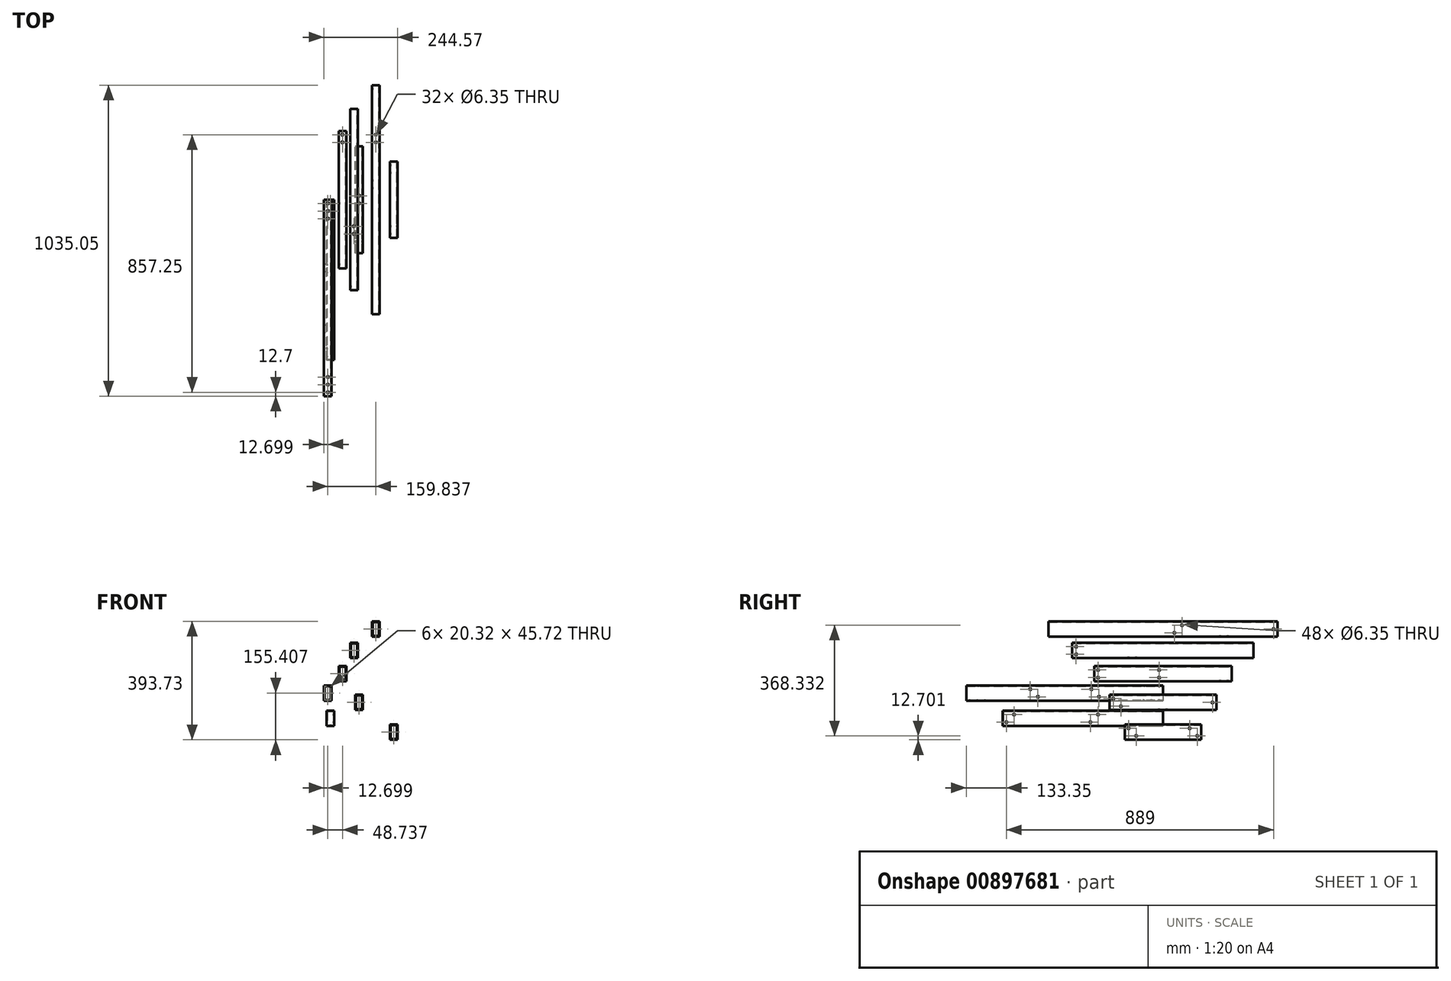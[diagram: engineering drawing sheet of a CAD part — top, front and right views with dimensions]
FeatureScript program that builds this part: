
annotation { "Feature Type Name" : "Feature", "Feature Type Description" : "" }
export const myFeature = defineFeature(function(context is Context, id is Id, definition is map)
    precondition{}
    {
        {
            var Q0;
            Q0=qCreatedBy(makeId("Front.planeOp"),FACE);
            var sketch = newSketch(context, id + "F0", { "sketchPlane" : qUnion([Q0])});
            skLineSegment(sketch, "E0.bottom", {"start": v(29.95, 32.2) * mm, "end": v(4.55, 32.2) * mm});
            skLineSegment(sketch, "E0.top", {"start": v(29.95, -18.6) * mm, "end": v(4.55, -18.6) * mm});
            skLineSegment(sketch, "E0.left", {"start": v(29.95, 32.2) * mm, "end": v(29.95, -18.6) * mm});
            skLineSegment(sketch, "E0.right", {"start": v(4.55, 32.2) * mm, "end": v(4.55, -18.6) * mm});
            skPoint(sketch, "E0.middle", {"position": v(17.25, 6.8) * mm});
            skSolve(sketch);
        }
        {
            var Q0;
            Q0 = qSketchRegion(id + "F0", true);
            extrude(context, id + "F1", {"entities" : qUnion([Q0]), "endBound" : BoundingType.SYMMETRIC, "depth" : 355.6 * mm, "offsetDistance" : 25.4 * mm});
        }
        {
            var Q0;
            Q0=makeQuery(id+"F1.opExtrude","CAP_FACE",FACE,{"disambiguationData":[OSD([sQuery(id+"F0.wireOp",EDGE,"E0.bottom"),sQuery(id+"F0.wireOp",EDGE,"E0.top"),sQuery(id+"F0.wireOp",EDGE,"E0.left"),sQuery(id+"F0.wireOp",EDGE,"E0.right")])],"isStart":false});
            var Q1;
            Q1=makeQuery(id+"F1.opExtrude","CAP_FACE",FACE,{"disambiguationData":[OSD([sQuery(id+"F0.wireOp",EDGE,"E0.bottom"),sQuery(id+"F0.wireOp",EDGE,"E0.top"),sQuery(id+"F0.wireOp",EDGE,"E0.left"),sQuery(id+"F0.wireOp",EDGE,"E0.right")])],"isStart":true});
            shell(context, id + "F2", {"entities" : qUnion([Q0, Q1]), "thickness" : 2.54 * mm});
        }
        {
            var Q0;
            Q0=qCreatedBy(makeId("Front.planeOp"),FACE);
            var sketch = newSketch(context, id + "F3", { "sketchPlane" : qUnion([Q0])});
            skLineSegment(sketch, "E1.bottom", {"start": v(-12.7, 205.12) * mm, "end": v(12.7, 205.12) * mm});
            skLineSegment(sketch, "E1.top", {"start": v(-12.7, 154.32) * mm, "end": v(12.7, 154.32) * mm});
            skLineSegment(sketch, "E1.left", {"start": v(-12.7, 205.12) * mm, "end": v(-12.7, 154.32) * mm});
            skLineSegment(sketch, "E1.right", {"start": v(12.7, 205.12) * mm, "end": v(12.7, 154.32) * mm});
            skPoint(sketch, "E1.middle", {"position": v(0, 179.72) * mm});
            skSolve(sketch);
        }
        {
            var Q0;
            Q0 = qSketchRegion(id + "F3", true);
            extrude(context, id + "F4", {"entities" : qUnion([Q0]), "endBound" : BoundingType.SYMMETRIC, "depth" : 603.25 * mm, "offsetDistance" : 25.4 * mm});
        }
        {
            var Q0;
            Q0=makeQuery(id+"F4.opExtrude","CAP_FACE",FACE,{"disambiguationData":[OSD([sQuery(id+"F3.wireOp",EDGE,"E1.bottom"),sQuery(id+"F3.wireOp",EDGE,"E1.top"),sQuery(id+"F3.wireOp",EDGE,"E1.left"),sQuery(id+"F3.wireOp",EDGE,"E1.right")])],"isStart":false});
            var Q1;
            Q1=makeQuery(id+"F4.opExtrude","CAP_FACE",FACE,{"disambiguationData":[OSD([sQuery(id+"F3.wireOp",EDGE,"E1.bottom"),sQuery(id+"F3.wireOp",EDGE,"E1.top"),sQuery(id+"F3.wireOp",EDGE,"E1.left"),sQuery(id+"F3.wireOp",EDGE,"E1.right")])],"isStart":true});
            shell(context, id + "F5", {"entities" : qUnion([Q0, Q1]), "thickness" : 2.54 * mm});
        }
        {
            var Q0;
            Q0=qCreatedBy(makeId("Front.planeOp"),FACE);
            var sketch = newSketch(context, id + "F6", { "sketchPlane" : qUnion([Q0])});
            skLineSegment(sketch, "E2.bottom", {"start": v(-25.48, 127.53) * mm, "end": v(-50.88, 127.53) * mm});
            skLineSegment(sketch, "E2.top", {"start": v(-25.48, 76.73) * mm, "end": v(-50.88, 76.73) * mm});
            skLineSegment(sketch, "E2.left", {"start": v(-25.48, 127.53) * mm, "end": v(-25.48, 76.73) * mm});
            skLineSegment(sketch, "E2.right", {"start": v(-50.88, 127.53) * mm, "end": v(-50.88, 76.73) * mm});
            skPoint(sketch, "E2.middle", {"position": v(-38.18, 102.13) * mm});
            skSolve(sketch);
        }
        {
            var Q0;
            Q0 = qSketchRegion(id + "F6", true);
            extrude(context, id + "F7", {"entities" : qUnion([Q0]), "endBound" : BoundingType.SYMMETRIC, "depth" : 457.2 * mm, "offsetDistance" : 25.4 * mm});
        }
        {
            var Q0;
            Q0=makeQuery(id+"F7.opExtrude","CAP_FACE",FACE,{"disambiguationData":[OSD([sQuery(id+"F6.wireOp",EDGE,"E2.bottom"),sQuery(id+"F6.wireOp",EDGE,"E2.top"),sQuery(id+"F6.wireOp",EDGE,"E2.left"),sQuery(id+"F6.wireOp",EDGE,"E2.right")])],"isStart":false});
            var Q1;
            Q1=makeQuery(id+"F7.opExtrude","CAP_FACE",FACE,{"disambiguationData":[OSD([sQuery(id+"F6.wireOp",EDGE,"E2.bottom"),sQuery(id+"F6.wireOp",EDGE,"E2.top"),sQuery(id+"F6.wireOp",EDGE,"E2.left"),sQuery(id+"F6.wireOp",EDGE,"E2.right")])],"isStart":true});
            shell(context, id + "F8", {"entities" : qUnion([Q0, Q1]), "thickness" : 2.54 * mm});
        }
        {
            var Q0;
            Q0=makeQuery(id+"F1.opExtrude","SWEPT_FACE",FACE,{"disambiguationData":[OSD([sQuery(id+"F0.wireOp",EDGE,"E0.left")])]});
            var sketch = newSketch(context, id + "F9", { "sketchPlane" : qUnion([Q0])});
            skCircle(sketch, "E3", {"center": v(-165.1, 19.5) * mm, "radius": 3.18 * mm});
            skCircle(sketch, "E4", {"center": v(-139.7, -5.9) * mm, "radius": 3.18 * mm});
            skCircle(sketch, "E5", {"center": v(165.1, 6.8) * mm, "radius": 3.18 * mm});
            skSolve(sketch);
        }
        {
            var Q0;
            Q0 = qSketchRegion(id + "F9", true);
            extrude(context, id + "F10", {"entities" : qUnion([Q0]), "operationType" : NewBodyOperationType.REMOVE, "endBound" : BoundingType.THROUGH_ALL, "oppositeDirection" : true, "depth" : 25.4 * mm, "offsetDistance" : 25.4 * mm});
        }
        {
            var Q0;
            Q0=makeQuery(id+"F1.opExtrude","SWEPT_FACE",FACE,{"disambiguationData":[OSD([sQuery(id+"F0.wireOp",EDGE,"E0.bottom")])]});
            var sketch = newSketch(context, id + "F11", { "sketchPlane" : qUnion([Q0])});
            skCircle(sketch, "E6", {"center": v(17.25, -12.7) * mm, "radius": 3.18 * mm});
            skCircle(sketch, "E7", {"center": v(17.25, 12.7) * mm, "radius": 3.18 * mm});
            skSolve(sketch);
        }
        {
            var Q0;
            Q0=makeQuery(id+"F11.imprint","IMPRINT",FACE,{"disambiguationData":[TD([[makeQuery(id+"F11.imprint","IMPRINT",EDGE,{"derivedFrom":sQuery(id+"F11.wireOp",EDGE,"E7")}),1.0]])]});
            var Q1;
            Q1=makeQuery(id+"F11.imprint","IMPRINT",FACE,{"disambiguationData":[TD([[makeQuery(id+"F11.imprint","IMPRINT",EDGE,{"derivedFrom":sQuery(id+"F11.wireOp",EDGE,"E6")}),1.0]])]});
            extrude(context, id + "F12", {"entities" : qUnion([Q0, Q1]), "operationType" : NewBodyOperationType.REMOVE, "endBound" : BoundingType.THROUGH_ALL, "oppositeDirection" : true, "depth" : 25.4 * mm, "offsetDistance" : 25.4 * mm});
        }
        {
            var Q0;
            Q0=makeQuery(id+"F4.opExtrude","SWEPT_FACE",FACE,{"disambiguationData":[OSD([sQuery(id+"F3.wireOp",EDGE,"E1.right")])]});
            var sketch = newSketch(context, id + "F13", { "sketchPlane" : qUnion([Q0])});
            skCircle(sketch, "E8", {"center": v(-288.93, 192.42) * mm, "radius": 3.18 * mm});
            skCircle(sketch, "E9", {"center": v(-288.93, 167.02) * mm, "radius": 3.18 * mm});
            skSolve(sketch);
        }
        {
            var Q0;
            Q0 = qSketchRegion(id + "F13", true);
            extrude(context, id + "F14", {"entities" : qUnion([Q0]), "operationType" : NewBodyOperationType.REMOVE, "endBound" : BoundingType.THROUGH_ALL, "oppositeDirection" : true, "depth" : 25.4 * mm, "offsetDistance" : 25.4 * mm});
        }
        {
            var Q0;
            Q0=makeQuery(id+"F4.opExtrude","SWEPT_FACE",FACE,{"disambiguationData":[OSD([sQuery(id+"F3.wireOp",EDGE,"E1.bottom")])]});
            var sketch = newSketch(context, id + "F15", { "sketchPlane" : qUnion([Q0])});
            skCircle(sketch, "E10", {"center": v(0, -114.3) * mm, "radius": 3.18 * mm});
            skCircle(sketch, "E11", {"center": v(0, -88.9) * mm, "radius": 3.18 * mm});
            skSolve(sketch);
        }
        {
            var Q0;
            Q0 = qSketchRegion(id + "F15", true);
            extrude(context, id + "F16", {"entities" : qUnion([Q0]), "operationType" : NewBodyOperationType.REMOVE, "endBound" : BoundingType.THROUGH_ALL, "oppositeDirection" : true, "depth" : 25.4 * mm, "offsetDistance" : 25.4 * mm});
        }
        {
            var Q0;
            Q0=makeQuery(id+"F7.opExtrude","SWEPT_FACE",FACE,{"disambiguationData":[OSD([sQuery(id+"F6.wireOp",EDGE,"E2.left")])]});
            var sketch = newSketch(context, id + "F17", { "sketchPlane" : qUnion([Q0])});
            skCircle(sketch, "E12", {"center": v(-215.9, 114.83) * mm, "radius": 3.18 * mm});
            skCircle(sketch, "E13", {"center": v(-215.9, 89.43) * mm, "radius": 3.18 * mm});
            skCircle(sketch, "E14", {"center": v(-12.7, 114.83) * mm, "radius": 3.18 * mm});
            skCircle(sketch, "E15", {"center": v(-12.7, 89.43) * mm, "radius": 3.18 * mm});
            skSolve(sketch);
        }
        {
            var Q0;
            Q0 = qSketchRegion(id + "F17", true);
            extrude(context, id + "F18", {"entities" : qUnion([Q0]), "operationType" : NewBodyOperationType.REMOVE, "endBound" : BoundingType.THROUGH_ALL, "oppositeDirection" : true, "depth" : 25.4 * mm, "offsetDistance" : 25.4 * mm});
        }
        {
            var Q0;
            Q0=makeQuery(id+"F7.opExtrude","SWEPT_FACE",FACE,{"disambiguationData":[OSD([sQuery(id+"F6.wireOp",EDGE,"E2.top")])]});
            var sketch = newSketch(context, id + "F19", { "sketchPlane" : qUnion([Q0])});
            skCircle(sketch, "E16", {"center": v(-38.18, -215.9) * mm, "radius": 3.18 * mm});
            skCircle(sketch, "E17", {"center": v(-38.18, -190.5) * mm, "radius": 3.18 * mm});
            skSolve(sketch);
        }
        {
            var Q0;
            Q0 = qSketchRegion(id + "F19", true);
            extrude(context, id + "F20", {"entities" : qUnion([Q0]), "operationType" : NewBodyOperationType.REMOVE, "endBound" : BoundingType.THROUGH_ALL, "oppositeDirection" : true, "depth" : 25.4 * mm, "offsetDistance" : 25.4 * mm});
        }
        {
            var Q0;
            Q0=qCreatedBy(makeId("Front.planeOp"),FACE);
            var sketch = newSketch(context, id + "F21", { "sketchPlane" : qUnion([Q0])});
            skLineSegment(sketch, "E18.bottom", {"start": v(85.62, 276.5) * mm, "end": v(60.22, 276.5) * mm});
            skLineSegment(sketch, "E18.top", {"start": v(85.62, 225.7) * mm, "end": v(60.22, 225.7) * mm});
            skLineSegment(sketch, "E18.left", {"start": v(85.62, 276.5) * mm, "end": v(85.62, 225.7) * mm});
            skLineSegment(sketch, "E18.right", {"start": v(60.22, 276.5) * mm, "end": v(60.22, 225.7) * mm});
            skPoint(sketch, "E18.middle", {"position": v(72.92, 251.1) * mm});
            skSolve(sketch);
        }
        {
            var Q0;
            Q0 = qSketchRegion(id + "F21", true);
            extrude(context, id + "F22", {"entities" : qUnion([Q0]), "endBound" : BoundingType.SYMMETRIC, "depth" : 762 * mm, "offsetDistance" : 25.4 * mm});
        }
        {
            var Q0;
            Q0=makeQuery(id+"F22.opExtrude","CAP_FACE",FACE,{"disambiguationData":[OSD([sQuery(id+"F21.wireOp",EDGE,"E18.bottom"),sQuery(id+"F21.wireOp",EDGE,"E18.top"),sQuery(id+"F21.wireOp",EDGE,"E18.left"),sQuery(id+"F21.wireOp",EDGE,"E18.right")])],"isStart":false});
            var Q1;
            Q1=makeQuery(id+"F22.opExtrude","CAP_FACE",FACE,{"disambiguationData":[OSD([sQuery(id+"F21.wireOp",EDGE,"E18.bottom"),sQuery(id+"F21.wireOp",EDGE,"E18.top"),sQuery(id+"F21.wireOp",EDGE,"E18.left"),sQuery(id+"F21.wireOp",EDGE,"E18.right")])],"isStart":true});
            shell(context, id + "F23", {"entities" : qUnion([Q0, Q1]), "thickness" : 2.54 * mm});
        }
        {
            var Q0;
            Q0=makeQuery(id+"F22.opExtrude","SWEPT_FACE",FACE,{"disambiguationData":[OSD([sQuery(id+"F21.wireOp",EDGE,"E18.left")])]});
            var sketch = newSketch(context, id + "F24", { "sketchPlane" : qUnion([Q0])});
            skCircle(sketch, "E19", {"center": v(368.3, 251.1) * mm, "radius": 3.18 * mm});
            skCircle(sketch, "E20", {"center": v(63.5, 263.8) * mm, "radius": 3.18 * mm});
            skCircle(sketch, "E21", {"center": v(38.1, 238.4) * mm, "radius": 3.18 * mm});
            skSolve(sketch);
        }
        {
            var Q0;
            Q0 = qSketchRegion(id + "F24", true);
            extrude(context, id + "F25", {"entities" : qUnion([Q0]), "operationType" : NewBodyOperationType.REMOVE, "endBound" : BoundingType.THROUGH_ALL, "oppositeDirection" : true, "depth" : 25.4 * mm, "offsetDistance" : 25.4 * mm});
        }
        {
            var Q0;
            Q0=makeQuery(id+"F22.opExtrude","SWEPT_FACE",FACE,{"disambiguationData":[OSD([sQuery(id+"F21.wireOp",EDGE,"E18.bottom")])]});
            var sketch = newSketch(context, id + "F26", { "sketchPlane" : qUnion([Q0])});
            skCircle(sketch, "E22", {"center": v(72.92, 215.9) * mm, "radius": 3.18 * mm});
            skCircle(sketch, "E23", {"center": v(72.92, 190.5) * mm, "radius": 3.18 * mm});
            skSolve(sketch);
        }
        {
            var Q0;
            Q0 = qSketchRegion(id + "F26", true);
            extrude(context, id + "F27", {"entities" : qUnion([Q0]), "operationType" : NewBodyOperationType.REMOVE, "endBound" : BoundingType.THROUGH_ALL, "oppositeDirection" : true, "depth" : 25.4 * mm, "offsetDistance" : 25.4 * mm});
        }
        {
            var Q0;
            Q0=qCreatedBy(makeId("Front.planeOp"),FACE);
            var sketch = newSketch(context, id + "F28", { "sketchPlane" : qUnion([Q0])});
            skLineSegment(sketch, "E24.bottom", {"start": v(119.55, -66.44) * mm, "end": v(144.95, -66.44) * mm});
            skLineSegment(sketch, "E24.top", {"start": v(119.55, -117.24) * mm, "end": v(144.95, -117.24) * mm});
            skLineSegment(sketch, "E24.left", {"start": v(119.55, -66.44) * mm, "end": v(119.55, -117.24) * mm});
            skLineSegment(sketch, "E24.right", {"start": v(144.95, -66.44) * mm, "end": v(144.95, -117.24) * mm});
            skPoint(sketch, "E24.middle", {"position": v(132.25, -91.84) * mm});
            skSolve(sketch);
        }
        {
            var Q0;
            Q0 = qSketchRegion(id + "F28", true);
            extrude(context, id + "F29", {"entities" : qUnion([Q0]), "endBound" : BoundingType.SYMMETRIC, "depth" : 254 * mm, "offsetDistance" : 25.4 * mm});
        }
        {
            var Q0;
            Q0=makeQuery(id+"F29.opExtrude","CAP_FACE",FACE,{"disambiguationData":[OSD([sQuery(id+"F28.wireOp",EDGE,"E24.bottom"),sQuery(id+"F28.wireOp",EDGE,"E24.top"),sQuery(id+"F28.wireOp",EDGE,"E24.left"),sQuery(id+"F28.wireOp",EDGE,"E24.right")])],"isStart":false});
            var Q1;
            Q1=makeQuery(id+"F29.opExtrude","CAP_FACE",FACE,{"disambiguationData":[OSD([sQuery(id+"F28.wireOp",EDGE,"E24.bottom"),sQuery(id+"F28.wireOp",EDGE,"E24.top"),sQuery(id+"F28.wireOp",EDGE,"E24.left"),sQuery(id+"F28.wireOp",EDGE,"E24.right")])],"isStart":true});
            shell(context, id + "F30", {"entities" : qUnion([Q0, Q1]), "thickness" : 2.54 * mm});
        }
        {
            var Q0;
            Q0=makeQuery(id+"F29.opExtrude","SWEPT_FACE",FACE,{"disambiguationData":[OSD([sQuery(id+"F28.wireOp",EDGE,"E24.right")])]});
            var sketch = newSketch(context, id + "F31", { "sketchPlane" : qUnion([Q0])});
            skCircle(sketch, "E25", {"center": v(-114.3, -79.14) * mm, "radius": 3.17 * mm});
            skCircle(sketch, "E26", {"center": v(-88.9, -104.54) * mm, "radius": 3.17 * mm});
            skCircle(sketch, "E27", {"center": v(88.9, -79.14) * mm, "radius": 3.17 * mm});
            skCircle(sketch, "E28", {"center": v(114.3, -104.54) * mm, "radius": 3.17 * mm});
            skSolve(sketch);
        }
        {
            var Q0;
            Q0 = qSketchRegion(id + "F31", true);
            extrude(context, id + "F32", {"entities" : qUnion([Q0]), "operationType" : NewBodyOperationType.REMOVE, "endBound" : BoundingType.THROUGH_ALL, "oppositeDirection" : true, "depth" : 25.4 * mm, "offsetDistance" : 25.4 * mm});
        }
        {
            var Q0;
            Q0=qCreatedBy(makeId("Front.planeOp"),FACE);
            var sketch = newSketch(context, id + "F33", { "sketchPlane" : qUnion([Q0])});
            skLineSegment(sketch, "E29.bottom", {"start": v(-90.63, -20.67) * mm, "end": v(-65.23, -20.67) * mm});
            skLineSegment(sketch, "E29.top", {"start": v(-90.63, -71.47) * mm, "end": v(-65.23, -71.47) * mm});
            skLineSegment(sketch, "E29.left", {"start": v(-90.63, -20.67) * mm, "end": v(-90.63, -71.47) * mm});
            skLineSegment(sketch, "E29.right", {"start": v(-65.23, -20.67) * mm, "end": v(-65.23, -71.47) * mm});
            skSolve(sketch);
        }
        {
            var Q0;
            Q0=makeQuery(id+"F33.imprint","IMPRINT",FACE,{"disambiguationData":[TD([[makeQuery(id+"F33.imprint","IMPRINT",EDGE,{"derivedFrom":sQuery(id+"F33.wireOp",EDGE,"E29.bottom")}),-1.0]])]});
            extrude(context, id + "F34", {"entities" : qUnion([Q0]), "depth" : 533.4 * mm, "offsetDistance" : 25.4 * mm});
        }
        {
            var Q0;
            Q0=makeQuery(id+"F34.opExtrude","CAP_FACE",FACE,{"disambiguationData":[OSD([sQuery(id+"F33.wireOp",EDGE,"E29.bottom"),sQuery(id+"F33.wireOp",EDGE,"E29.top"),sQuery(id+"F33.wireOp",EDGE,"E29.left"),sQuery(id+"F33.wireOp",EDGE,"E29.right")])],"isStart":true});
            shell(context, id + "F35", {"entities" : qUnion([Q0]), "thickness" : 2.54 * mm});
        }
        {
            var Q0;
            Q0=qCreatedBy(makeId("Front.planeOp"),FACE);
            var sketch = newSketch(context, id + "F36", { "sketchPlane" : qUnion([Q0])});
            skLineSegment(sketch, "E30.bottom", {"start": v(-99.62, 63.57) * mm, "end": v(-74.22, 63.57) * mm});
            skLineSegment(sketch, "E30.top", {"start": v(-99.62, 12.77) * mm, "end": v(-74.22, 12.77) * mm});
            skLineSegment(sketch, "E30.left", {"start": v(-99.62, 63.57) * mm, "end": v(-99.62, 12.77) * mm});
            skLineSegment(sketch, "E30.right", {"start": v(-74.22, 63.57) * mm, "end": v(-74.22, 12.77) * mm});
            skSolve(sketch);
        }
        {
            var Q0;
            Q0=makeQuery(id+"F36.imprint","IMPRINT",FACE,{"disambiguationData":[TD([[makeQuery(id+"F36.imprint","IMPRINT",EDGE,{"derivedFrom":sQuery(id+"F36.wireOp",EDGE,"E30.bottom")}),-1.0]])]});
            extrude(context, id + "F37", {"entities" : qUnion([Q0]), "depth" : 654.05 * mm, "offsetDistance" : 25.4 * mm});
        }
        {
            var Q0;
            Q0=makeQuery(id+"F37.opExtrude","CAP_FACE",FACE,{"disambiguationData":[OSD([sQuery(id+"F36.wireOp",EDGE,"E30.bottom"),sQuery(id+"F36.wireOp",EDGE,"E30.top"),sQuery(id+"F36.wireOp",EDGE,"E30.left"),sQuery(id+"F36.wireOp",EDGE,"E30.right")])],"isStart":true});
            var Q1;
            Q1=makeQuery(id+"F37.opExtrude","CAP_FACE",FACE,{"disambiguationData":[OSD([sQuery(id+"F36.wireOp",EDGE,"E30.bottom"),sQuery(id+"F36.wireOp",EDGE,"E30.top"),sQuery(id+"F36.wireOp",EDGE,"E30.left"),sQuery(id+"F36.wireOp",EDGE,"E30.right")])],"isStart":false});
            shell(context, id + "F38", {"entities" : qUnion([Q0, Q1]), "thickness" : 2.54 * mm});
        }
        {
            var Q0;
            Q0=makeQuery(id+"F37.opExtrude","SWEPT_FACE",FACE,{"disambiguationData":[OSD([sQuery(id+"F36.wireOp",EDGE,"E30.bottom")])]});
            var sketch = newSketch(context, id + "F39", { "sketchPlane" : qUnion([Q0])});
            skCircle(sketch, "E31", {"center": v(-86.92, -12.7) * mm, "radius": 3.18 * mm});
            skCircle(sketch, "E32", {"center": v(-86.92, -38.1) * mm, "radius": 3.18 * mm});
            skSolve(sketch);
        }
        {
            var Q0;
            Q0=sQuery(id+"F39.wireOp",VERTEX,"E32.center");
            var Q1;
            Q1=sQuery(id+"F39.wireOp",VERTEX,"E31.center");
            var Q2;
            Q2=makeQuery(id+"F37.opExtrude","SWEPT_BODY",BODY,{"disambiguationData":[OSD([sQuery(id+"F36.wireOp",EDGE,"E30.bottom"),sQuery(id+"F36.wireOp",EDGE,"E30.top"),sQuery(id+"F36.wireOp",EDGE,"E30.left"),sQuery(id+"F36.wireOp",EDGE,"E30.right")])]});
            hole(context, id + "F40", {"style" : HoleStyle.SIMPLE, "endStyle" : HoleEndStyle.BLIND, "holeDiameter" : 6.35 * mm, "majorDiameter" : 6.35 * mm, "holeDepth" : 50.8 * mm, "isTappedThrough" : true, "tappedDepth" : 12.7 * mm, "tapClearance" : 3, "locations" : qUnion([Q0, Q1]), "scope" : qUnion([Q2])});
        }
        {
            var Q0;
            Q0=makeQuery(id+"F34.opExtrude","SWEPT_FACE",FACE,{"disambiguationData":[OSD([sQuery(id+"F33.wireOp",EDGE,"E29.top")])]});
            var sketch = newSketch(context, id + "F41", { "sketchPlane" : qUnion([Q0])});
            skCircle(sketch, "E33", {"center": v(-77.93, 12.7) * mm, "radius": 3.18 * mm});
            skCircle(sketch, "E34", {"center": v(-77.93, 38.1) * mm, "radius": 3.18 * mm});
            skSolve(sketch);
        }
        {
            var Q0;
            Q0=sQuery(id+"F41.wireOp",VERTEX,"E33.center");
            var Q1;
            Q1=sQuery(id+"F41.wireOp",VERTEX,"E34.center");
            var Q2;
            Q2=makeQuery(id+"F34.opExtrude","SWEPT_BODY",BODY,{"disambiguationData":[OSD([sQuery(id+"F33.wireOp",EDGE,"E29.bottom"),sQuery(id+"F33.wireOp",EDGE,"E29.top"),sQuery(id+"F33.wireOp",EDGE,"E29.left"),sQuery(id+"F33.wireOp",EDGE,"E29.right")])]});
            hole(context, id + "F42", {"style" : HoleStyle.SIMPLE, "endStyle" : HoleEndStyle.BLIND, "holeDiameter" : 6.35 * mm, "majorDiameter" : 6.35 * mm, "holeDepth" : 50.8 * mm, "isTappedThrough" : true, "tappedDepth" : 12.7 * mm, "tapClearance" : 3, "locations" : qUnion([Q0, Q1]), "scope" : qUnion([Q2])});
        }
        {
            var Q0;
            Q0=makeQuery(id+"F37.opExtrude","SWEPT_FACE",FACE,{"disambiguationData":[OSD([sQuery(id+"F36.wireOp",EDGE,"E30.top")])]});
            var sketch = newSketch(context, id + "F43", { "sketchPlane" : qUnion([Q0])});
            skCircle(sketch, "E35", {"center": v(-86.92, 641.35) * mm, "radius": 3.18 * mm});
            skCircle(sketch, "E36", {"center": v(-86.92, 615.95) * mm, "radius": 3.18 * mm});
            skCircle(sketch, "E37", {"center": v(-86.92, 590.55) * mm, "radius": 3.18 * mm});
            skCircle(sketch, "E38", {"center": v(-86.92, 63.5) * mm, "radius": 3.18 * mm});
            skSolve(sketch);
        }
        {
            var Q0;
            Q0=sQuery(id+"F43.wireOp",VERTEX,"E36.center");
            var Q1;
            Q1=sQuery(id+"F43.wireOp",VERTEX,"E35.center");
            var Q2;
            Q2=makeQuery(id+"F37.opExtrude","SWEPT_BODY",BODY,{"disambiguationData":[OSD([sQuery(id+"F36.wireOp",EDGE,"E30.bottom"),sQuery(id+"F36.wireOp",EDGE,"E30.top"),sQuery(id+"F36.wireOp",EDGE,"E30.left"),sQuery(id+"F36.wireOp",EDGE,"E30.right")])]});
            hole(context, id + "F44", {"style" : HoleStyle.SIMPLE, "endStyle" : HoleEndStyle.BLIND, "holeDiameter" : 6.35 * mm, "majorDiameter" : 6.35 * mm, "holeDepth" : 50.8 * mm, "isTappedThrough" : true, "tappedDepth" : 12.7 * mm, "tapClearance" : 3, "locations" : qUnion([Q0, Q1]), "scope" : qUnion([Q2])});
        }
        {
            var Q0;
            Q0=makeQuery(id+"F34.opExtrude","SWEPT_FACE",FACE,{"disambiguationData":[OSD([sQuery(id+"F33.wireOp",EDGE,"E29.left")])]});
            var sketch = newSketch(context, id + "F45", { "sketchPlane" : qUnion([Q0])});
            skLineSegment(sketch, "E39.bottom", {"start": v(533.4, -20.67) * mm, "end": v(203.2, -20.67) * mm});
            skLineSegment(sketch, "E39.top", {"start": v(533.4, -71.47) * mm, "end": v(203.2, -71.47) * mm});
            skLineSegment(sketch, "E39.left", {"start": v(533.4, -20.67) * mm, "end": v(533.4, -71.47) * mm});
            skLineSegment(sketch, "E39.right", {"start": v(203.2, -20.67) * mm, "end": v(203.2, -71.47) * mm});
            skSolve(sketch);
        }
        {
            var Q0;
            Q0=makeQuery(id+"F45.imprint","IMPRINT",FACE,{"disambiguationData":[TD([[makeQuery(id+"F45.imprint","IMPRINT",EDGE,{"derivedFrom":sQuery(id+"F45.wireOp",EDGE,"E39.bottom")}),1.0]])]});
            var sketch = newSketch(context, id + "F46", { "sketchPlane" : qUnion([Q0])});
            skCircle(sketch, "E40", {"center": v(215.9, -33.37) * mm, "radius": 3.18 * mm});
            skCircle(sketch, "E41", {"center": v(520.7, -58.77) * mm, "radius": 3.18 * mm});
            skCircle(sketch, "E42", {"center": v(495.3, -33.37) * mm, "radius": 3.18 * mm});
            skCircle(sketch, "E43", {"center": v(241.3, -58.77) * mm, "radius": 3.18 * mm});
            skSolve(sketch);
        }
        {
            var Q0;
            Q0=sQuery(id+"F46.wireOp",VERTEX,"E40.center");
            var Q1;
            Q1=sQuery(id+"F46.wireOp",VERTEX,"E43.center");
            var Q2;
            Q2=sQuery(id+"F46.wireOp",VERTEX,"E42.center");
            var Q3;
            Q3=sQuery(id+"F46.wireOp",VERTEX,"E41.center");
            var Q4;
            Q4=makeQuery(id+"F34.opExtrude","SWEPT_BODY",BODY,{"disambiguationData":[OSD([sQuery(id+"F33.wireOp",EDGE,"E29.bottom"),sQuery(id+"F33.wireOp",EDGE,"E29.top"),sQuery(id+"F33.wireOp",EDGE,"E29.left"),sQuery(id+"F33.wireOp",EDGE,"E29.right")])]});
            hole(context, id + "F47", {"style" : HoleStyle.SIMPLE, "endStyle" : HoleEndStyle.BLIND, "holeDiameter" : 6.35 * mm, "majorDiameter" : 6.35 * mm, "holeDepth" : 50.8 * mm, "isTappedThrough" : true, "tappedDepth" : 12.7 * mm, "tapClearance" : 3, "locations" : qUnion([Q0, Q1, Q2, Q3]), "scope" : qUnion([Q4])});
        }
        {
            var Q0;
            Q0=makeQuery(id+"F37.opExtrude","SWEPT_FACE",FACE,{"disambiguationData":[OSD([sQuery(id+"F36.wireOp",EDGE,"E30.left")])]});
            var sketch = newSketch(context, id + "F48", { "sketchPlane" : qUnion([Q0])});
            skCircle(sketch, "E44", {"center": v(212.73, 25.47) * mm, "radius": 3.18 * mm});
            skCircle(sketch, "E45", {"center": v(238.13, 50.87) * mm, "radius": 3.18 * mm});
            skCircle(sketch, "E46", {"center": v(441.32, 50.87) * mm, "radius": 3.18 * mm});
            skCircle(sketch, "E47", {"center": v(415.93, 25.47) * mm, "radius": 3.18 * mm});
            skSolve(sketch);
        }
        {
            var Q0;
            Q0=sQuery(id+"F48.wireOp",VERTEX,"E44.center");
            var Q1;
            Q1=makeQuery(id+"F37.opExtrude","SWEPT_BODY",BODY,{"disambiguationData":[OSD([sQuery(id+"F36.wireOp",EDGE,"E30.bottom"),sQuery(id+"F36.wireOp",EDGE,"E30.top"),sQuery(id+"F36.wireOp",EDGE,"E30.left"),sQuery(id+"F36.wireOp",EDGE,"E30.right")])]});
            hole(context, id + "F49", {"style" : HoleStyle.SIMPLE, "endStyle" : HoleEndStyle.BLIND, "holeDiameter" : 6.35 * mm, "majorDiameter" : 6.35 * mm, "holeDepth" : 50.8 * mm, "isTappedThrough" : true, "tappedDepth" : 12.7 * mm, "tapClearance" : 3, "locations" : qUnion([Q0]), "scope" : qUnion([Q1])});
        }
        {
            var Q0;
            Q0=sQuery(id+"F48.wireOp",VERTEX,"E45.center");
            var Q1;
            Q1=sQuery(id+"F48.wireOp",VERTEX,"E46.center");
            var Q2;
            Q2=sQuery(id+"F48.wireOp",VERTEX,"E47.center");
            var Q3;
            Q3=makeQuery(id+"F37.opExtrude","SWEPT_BODY",BODY,{"disambiguationData":[OSD([sQuery(id+"F36.wireOp",EDGE,"E30.bottom"),sQuery(id+"F36.wireOp",EDGE,"E30.top"),sQuery(id+"F36.wireOp",EDGE,"E30.left"),sQuery(id+"F36.wireOp",EDGE,"E30.right")])]});
            hole(context, id + "F50", {"style" : HoleStyle.SIMPLE, "endStyle" : HoleEndStyle.BLIND, "holeDiameter" : 6.35 * mm, "majorDiameter" : 6.35 * mm, "holeDepth" : 50.8 * mm, "isTappedThrough" : true, "tappedDepth" : 12.7 * mm, "tapClearance" : 3, "locations" : qUnion([Q0, Q1, Q2]), "scope" : qUnion([Q3])});
        }
        {
            var Q0;
            Q0=sQuery(id+"F43.wireOp",VERTEX,"E37.center");
            var Q1;
            Q1=makeQuery(id+"F37.opExtrude","SWEPT_BODY",BODY,{"disambiguationData":[OSD([sQuery(id+"F36.wireOp",EDGE,"E30.bottom"),sQuery(id+"F36.wireOp",EDGE,"E30.top"),sQuery(id+"F36.wireOp",EDGE,"E30.left"),sQuery(id+"F36.wireOp",EDGE,"E30.right")])]});
            hole(context, id + "F51", {"style" : HoleStyle.SIMPLE, "endStyle" : HoleEndStyle.BLIND, "holeDiameter" : 6.35 * mm, "majorDiameter" : 6.35 * mm, "holeDepth" : 50.8 * mm, "isTappedThrough" : true, "tappedDepth" : 12.7 * mm, "tapClearance" : 3, "locations" : qUnion([Q0]), "scope" : qUnion([Q1])});
        }
        {
            var Q0;
            Q0=sQuery(id+"F43.wireOp",VERTEX,"E38.center");
            var Q1;
            Q1=makeQuery(id+"F37.opExtrude","SWEPT_BODY",BODY,{"disambiguationData":[OSD([sQuery(id+"F36.wireOp",EDGE,"E30.bottom"),sQuery(id+"F36.wireOp",EDGE,"E30.top"),sQuery(id+"F36.wireOp",EDGE,"E30.left"),sQuery(id+"F36.wireOp",EDGE,"E30.right")])]});
            hole(context, id + "F52", {"style" : HoleStyle.SIMPLE, "endStyle" : HoleEndStyle.BLIND, "holeDiameter" : 6.35 * mm, "majorDiameter" : 6.35 * mm, "holeDepth" : 50.8 * mm, "isTappedThrough" : true, "tappedDepth" : 12.7 * mm, "tapClearance" : 3, "startFromSketch" : true, "locations" : qUnion([Q0]), "scope" : qUnion([Q1])});
        }
    });
